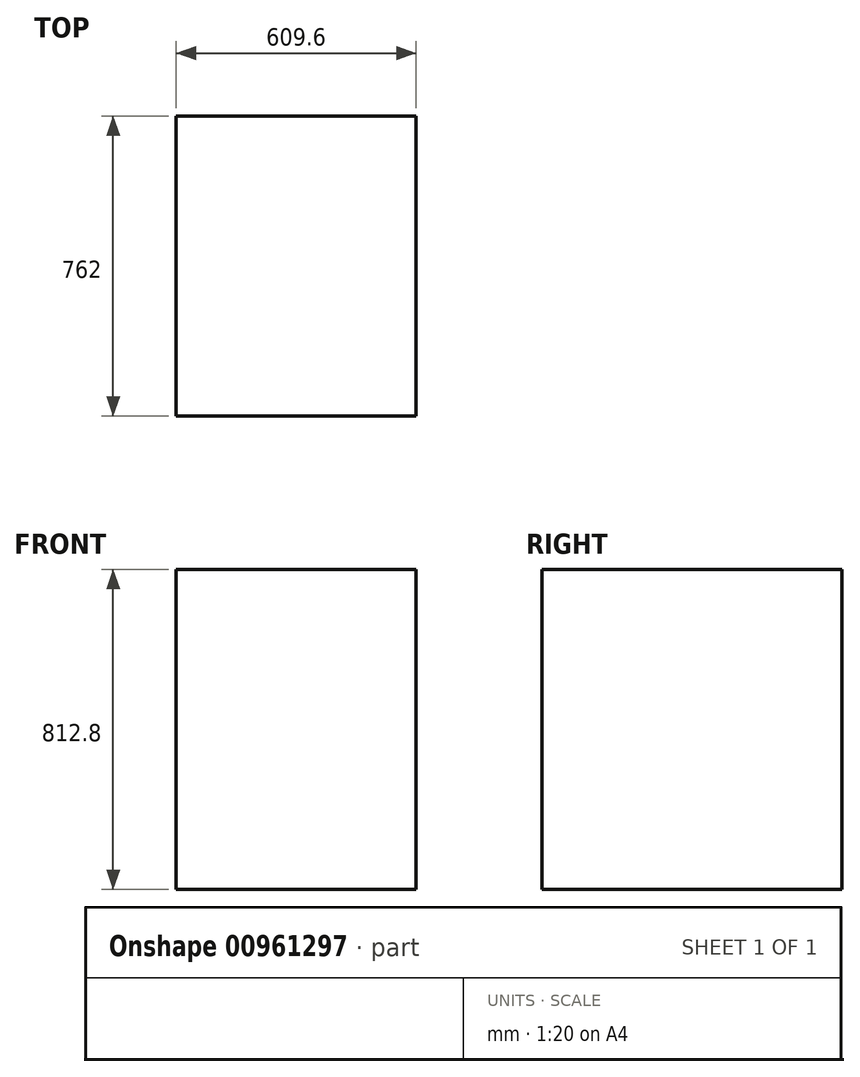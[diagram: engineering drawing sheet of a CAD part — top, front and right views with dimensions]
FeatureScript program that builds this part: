
annotation { "Feature Type Name" : "Feature", "Feature Type Description" : "" }
export const myFeature = defineFeature(function(context is Context, id is Id, definition is map)
    precondition{}
    {
        {
            var Q0;
            Q0=qCreatedBy(makeId("Right.planeOp"),FACE);
            var sketch = newSketch(context, id + "F0", { "sketchPlane" : qUnion([Q0])});
            skLineSegment(sketch, "E0.bottom", {"start": v(0, 0) * mm, "end": v(-762, 0) * mm});
            skLineSegment(sketch, "E0.top", {"start": v(0, 812.8) * mm, "end": v(-762, 812.8) * mm});
            skLineSegment(sketch, "E0.left", {"start": v(0, 0) * mm, "end": v(0, 812.8) * mm});
            skLineSegment(sketch, "E0.right", {"start": v(-762, 0) * mm, "end": v(-762, 812.8) * mm});
            skSolve(sketch);
        }
        {
            var Q0;
            Q0=makeQuery(id+"F0.imprint","IMPRINT",FACE,{"disambiguationData":[TD([[makeQuery(id+"F0.imprint","IMPRINT",EDGE,{"derivedFrom":sQuery(id+"F0.wireOp",EDGE,"E0.bottom")}),-1.0]])]});
            extrude(context, id + "F1", {"entities" : qUnion([Q0]), "oppositeDirection" : true, "depth" : 609.6 * mm, "offsetDistance" : 25.4 * mm});
        }
    });
